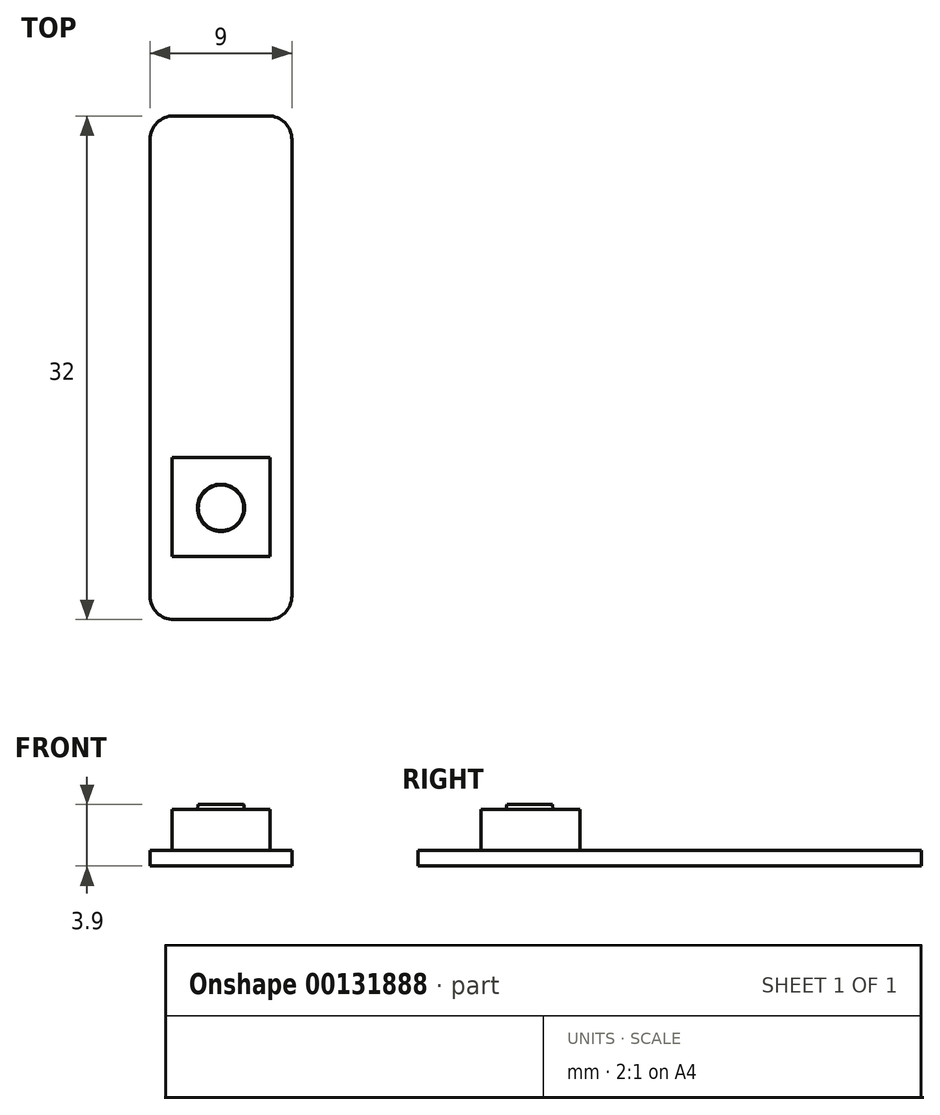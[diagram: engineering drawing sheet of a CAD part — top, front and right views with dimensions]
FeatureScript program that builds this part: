
annotation { "Feature Type Name" : "Feature", "Feature Type Description" : "" }
export const myFeature = defineFeature(function(context is Context, id is Id, definition is map)
    precondition{}
    {
        {
            var Q0;
            Q0=qCreatedBy(makeId("Top.planeOp"),FACE);
            var sketch = newSketch(context, id + "F0", { "sketchPlane" : qUnion([Q0])});
            skLineSegment(sketch, "E0.bottom", {"start": v(-4.5, 16) * mm, "end": v(4.5, 16) * mm});
            skLineSegment(sketch, "E0.top", {"start": v(-4.5, -16) * mm, "end": v(4.5, -16) * mm});
            skLineSegment(sketch, "E0.left", {"start": v(-4.5, 16) * mm, "end": v(-4.5, -16) * mm});
            skLineSegment(sketch, "E0.right", {"start": v(4.5, 16) * mm, "end": v(4.5, -16) * mm});
            skPoint(sketch, "E0.middle", {"position": v(0, 0) * mm});
            skSolve(sketch);
        }
        {
            var Q0;
            Q0 = qSketchRegion(id + "F0", true);
            extrude(context, id + "F1", {"entities" : qUnion([Q0]), "depth" : 1 * mm});
        }
        {
            var Q0;
            Q0=makeQuery(id+"F1.opExtrude","CAP_FACE",FACE,{"disambiguationData":[OSD([sQuery(id+"F0.wireOp",EDGE,"E0.bottom"),sQuery(id+"F0.wireOp",EDGE,"E0.top"),sQuery(id+"F0.wireOp",EDGE,"E0.left"),sQuery(id+"F0.wireOp",EDGE,"E0.right")])],"isStart":false});
            var sketch = newSketch(context, id + "F2", { "sketchPlane" : qUnion([Q0])});
            skLineSegment(sketch, "E1.bottom", {"start": v(-3.1, -5.7) * mm, "end": v(3.1, -5.7) * mm});
            skLineSegment(sketch, "E1.top", {"start": v(-3.1, -12) * mm, "end": v(3.1, -12) * mm});
            skLineSegment(sketch, "E1.left", {"start": v(-3.1, -5.7) * mm, "end": v(-3.1, -12) * mm});
            skLineSegment(sketch, "E1.right", {"start": v(3.1, -5.7) * mm, "end": v(3.1, -12) * mm});
            skPoint(sketch, "E1.middle", {"position": v(0, -8.85) * mm});
            skSolve(sketch);
        }
        {
            var Q0;
            Q0 = qSketchRegion(id + "F2", true);
            extrude(context, id + "F3", {"entities" : qUnion([Q0]), "operationType" : NewBodyOperationType.ADD, "depth" : 2.6 * mm});
        }
        {
            var Q0;
            Q0=makeQuery(id+"F3.opExtrude","CAP_FACE",FACE,{"disambiguationData":[OSD([sQuery(id+"F2.wireOp",EDGE,"E1.bottom"),sQuery(id+"F2.wireOp",EDGE,"E1.top"),sQuery(id+"F2.wireOp",EDGE,"E1.left"),sQuery(id+"F2.wireOp",EDGE,"E1.right")])],"isStart":false});
            var sketch = newSketch(context, id + "F4", { "sketchPlane" : qUnion([Q0])});
            skCircle(sketch, "E2", {"center": v(0, -8.9) * mm, "radius": 1.5 * mm});
            skPoint(sketch, "E2.centerSnap0", {"position": v(0, -12) * mm});
            skSolve(sketch);
        }
        {
            var Q0;
            Q0 = qSketchRegion(id + "F4", true);
            extrude(context, id + "F5", {"entities" : qUnion([Q0]), "operationType" : NewBodyOperationType.ADD, "depth" : 0.3 * mm, "hasDraft" : true, "draftAngle" : 10 * degree, "draftPullDirection" : true});
        }
        {
            var Q0;
            Q0=makeQuery(id+"F1.opExtrude","SWEPT_EDGE",EDGE,{"disambiguationData":[OSD([sQuery(id+"F0.wireOp",EDGE,"E0.top"),sQuery(id+"F0.wireOp",EDGE,"E0.right")])]});
            var Q1;
            Q1=makeQuery(id+"F1.opExtrude","SWEPT_EDGE",EDGE,{"disambiguationData":[OSD([sQuery(id+"F0.wireOp",EDGE,"E0.top"),sQuery(id+"F0.wireOp",EDGE,"E0.left")])]});
            var Q2;
            Q2=makeQuery(id+"F1.opExtrude","SWEPT_EDGE",EDGE,{"disambiguationData":[OSD([sQuery(id+"F0.wireOp",EDGE,"E0.bottom"),sQuery(id+"F0.wireOp",EDGE,"E0.right")])]});
            var Q3;
            Q3=makeQuery(id+"F1.opExtrude","SWEPT_EDGE",EDGE,{"disambiguationData":[OSD([sQuery(id+"F0.wireOp",EDGE,"E0.bottom"),sQuery(id+"F0.wireOp",EDGE,"E0.left")])]});
            fillet(context, id + "F6", {"entities" : qUnion([Q0, Q1, Q2, Q3]), "radius" : 1.5 * mm, "tangentPropagation" : true, "allowEdgeOverflow" : false});
        }
    });
